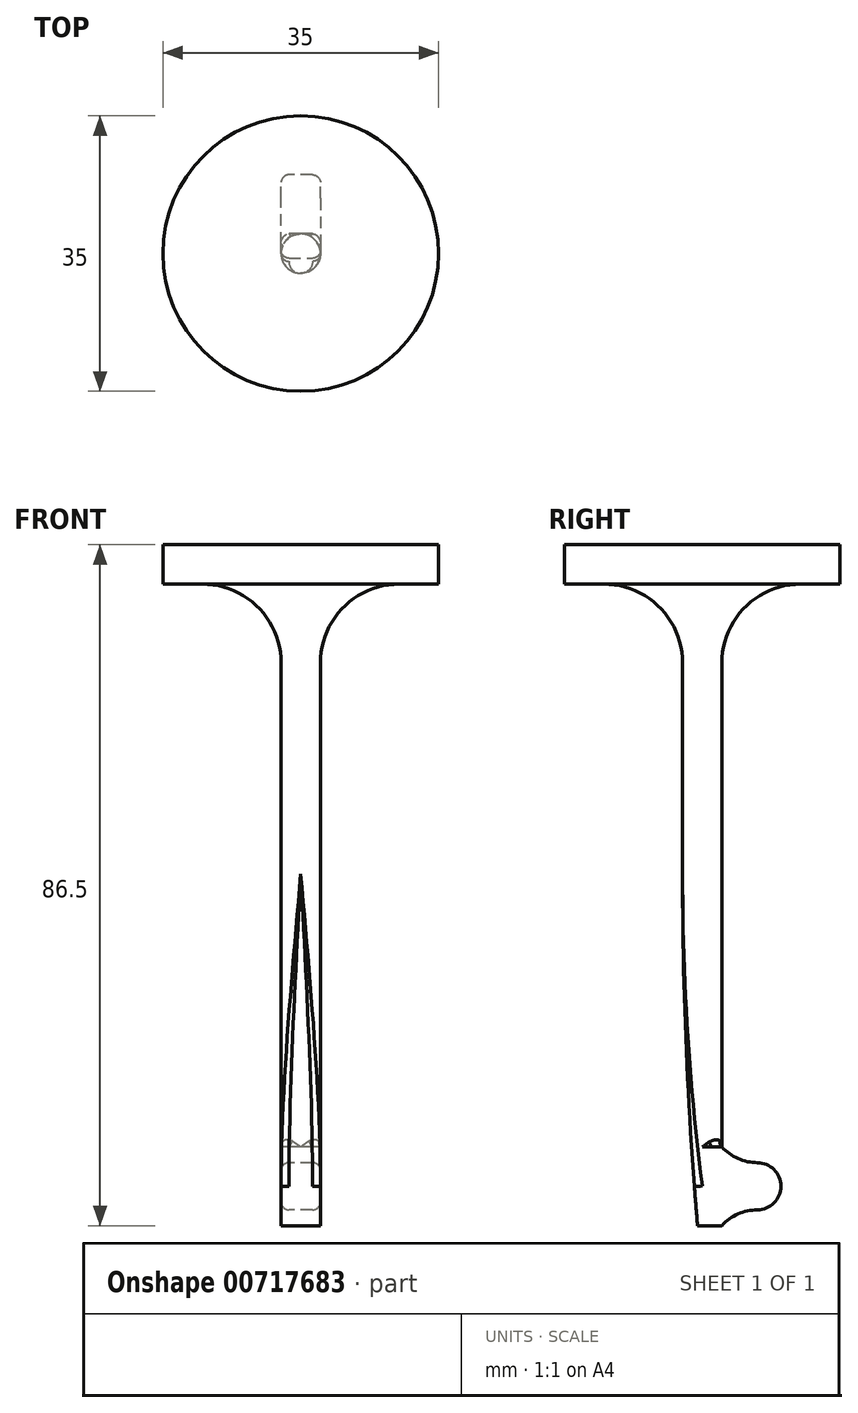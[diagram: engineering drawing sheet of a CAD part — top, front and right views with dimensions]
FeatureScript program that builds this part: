
annotation { "Feature Type Name" : "Feature", "Feature Type Description" : "" }
export const myFeature = defineFeature(function(context is Context, id is Id, definition is map)
    precondition{}
    {
        {
            assignVariable(context, id + "F0", {"name" : "Daxe", "anyValue" : 5});
        }
        {
            var Q0;
            Q0=qCreatedBy(makeId("Front.planeOp"),FACE);
            var sketch = newSketch(context, id + "F1", { "sketchPlane" : qUnion([Q0])});
            skLineSegment(sketch, "E0", {"start": v(-2.5, 81.5) * mm, "end": v(-17.5, 81.5) * mm});
            skLineSegment(sketch, "E1", {"start": v(-17.5, 81.5) * mm, "end": v(-17.5, 86.5) * mm});
            skLineSegment(sketch, "E2", {"start": v(-17.5, 86.5) * mm, "end": v(0, 86.5) * mm});
            skLineSegment(sketch, "E3", {"start": v(0, 86.5) * mm, "end": v(0, 0) * mm});
            skLineSegment(sketch, "E4", {"start": v(0, 0) * mm, "end": v(-2.5, 0) * mm});
            skLineSegment(sketch, "E5", {"start": v(-2.5, 0) * mm, "end": v(-2.5, 81.5) * mm});
            skSolve(sketch);
        }
        {
            var Q0;
            Q0=makeQuery(id+"F1.imprint","IMPRINT",FACE,{"disambiguationData":[TD([[makeQuery(id+"F1.imprint","IMPRINT",EDGE,{"derivedFrom":sQuery(id+"F1.wireOp",EDGE,"E0")}),-1.0]])]});
            var Q1;
            Q1=sQuery(id+"F1.wireOp",EDGE,"E3");
            revolve(context, id + "F2", {"surfaceOperationType" : NewSurfaceOperationType.NEW, "entities" : qUnion([Q0]), "axis" : qUnion([Q1]), "revolveType" : RevolveType.FULL});
        }
        {
            var Q0;
            Q0=qCreatedBy(makeId("Right.planeOp"),FACE);
            var sketch = newSketch(context, id + "F3", { "sketchPlane" : qUnion([Q0])});
            skArc(sketch, "E6", {"start": v(2.5, 10) * mm, "mid": v(4.54, 8.52) * mm, "end": v(7, 8) * mm});
            skArc(sketch, "E7", {"start": v(10, 5) * mm, "mid": v(9.12, 7.12) * mm, "end": v(7, 8) * mm});
            skLineSegment(sketch, "E8", {"start": v(0, 5) * mm, "end": v(10, 5) * mm, "construction": true});
            skLineSegment(sketch, "E9", {"start": v(2.5, 89) * mm, "end": v(2.5, 0) * mm, "construction": true});
            skLineSegment(sketch, "E10", {"start": v(-2.5, 0) * mm, "end": v(-2.5, 89) * mm, "construction": true});
            skArc(sketch, "E11.MirrorCS", {"start": v(10, 5) * mm, "mid": v(9.12, 2.88) * mm, "end": v(7, 2) * mm});
            skArc(sketch, "E12.MirrorCS", {"start": v(2.5, 0) * mm, "mid": v(4.54, 1.48) * mm, "end": v(7, 2) * mm});
            skLineSegment(sketch, "E13", {"start": v(2.5, 10) * mm, "end": v(0, 10) * mm});
            skLineSegment(sketch, "E14", {"start": v(0, 10) * mm, "end": v(0, 0) * mm});
            skLineSegment(sketch, "E15", {"start": v(0, 0) * mm, "end": v(2.5, 0) * mm});
            skSolve(sketch);
        }
        {
            var Q0;
            Q0=makeQuery(id+"F3.imprint","IMPRINT",FACE,{"disambiguationData":[TD([[makeQuery(id+"F3.imprint","IMPRINT",EDGE,{"derivedFrom":sQuery(id+"F3.wireOp",EDGE,"E6")}),-1.0]])]});
            extrude(context, id + "F4", {"entities" : qUnion([Q0]), "operationType" : NewBodyOperationType.ADD, "endBound" : BoundingType.SYMMETRIC, "depth" : (getVariable(context, 'Daxe')) * mm, "offsetDistance" : 25 * mm});
        }
        {
            var Q0;
            Q0=makeQuery(id+"F4.opExtrude","CAP_EDGE",EDGE,{"disambiguationData":[OSD([sQuery(id+"F3.wireOp",EDGE,"E6")])],"isStart":false});
            var Q1;
            Q1=makeQuery(id+"F4.opExtrude","CAP_EDGE",EDGE,{"disambiguationData":[OSD([sQuery(id+"F3.wireOp",EDGE,"E7"),sQuery(id+"F3.wireOp",EDGE,"E11.MirrorCS")])],"isStart":false});
            var Q2;
            Q2=makeQuery(id+"F4.opExtrude","CAP_EDGE",EDGE,{"disambiguationData":[OSD([sQuery(id+"F3.wireOp",EDGE,"E6")])],"isStart":true});
            fillet(context, id + "F5", {"entities" : qUnion([Q0, Q1, Q2]), "radius" : 1 * mm, "tangentPropagation" : true, "allowEdgeOverflow" : false});
        }
        {
            var Q0;
            Q0=makeQuery(id+"F2.opRevolve","SWEPT_EDGE",EDGE,{"disambiguationData":[OSD([sQuery(id+"F1.wireOp",EDGE,"E0"),sQuery(id+"F1.wireOp",EDGE,"E5")])]});
            fillet(context, id + "F6", {"entities" : qUnion([Q0]), "radius" : 10 * mm, "tangentPropagation" : true, "allowEdgeOverflow" : false});
        }
        {
            var Q0;
            Q0=qCreatedBy(makeId("Right.planeOp"),FACE);
            var sketch = newSketch(context, id + "F7", { "sketchPlane" : qUnion([Q0])});
            skArc(sketch, "E16", {"start": v(2.5, 10) * mm, "mid": v(4.54, 8.52) * mm, "end": v(7, 8) * mm});
            skArc(sketch, "E17", {"start": v(7, 2) * mm, "mid": v(10, 5) * mm, "end": v(7, 8) * mm});
            skArc(sketch, "E18", {"start": v(7, 2) * mm, "mid": v(4.54, 1.48) * mm, "end": v(2.5, 0) * mm});
            skSolve(sketch);
        }
        {
            var Q0;
            Q0=makeQuery(id+"F4.boolean.opBoolean","INTERSECT",EDGE,{"disambiguationData":[OD(1.0)],"derivedFrom":[makeQuery(id+"F2.opRevolve","SWEPT_FACE",FACE,{"disambiguationData":[OSD([sQuery(id+"F1.wireOp",EDGE,"E5")])]}),makeQuery(id+"F4.opExtrude","SWEPT_FACE",FACE,{"disambiguationData":[OSD([sQuery(id+"F3.wireOp",EDGE,"E13")])]})]});
            fillet(context, id + "F8", {"entities" : qUnion([Q0]), "radius" : 1 * mm, "tangentPropagation" : true, "allowEdgeOverflow" : false});
        }
        {
            var Q0;
            Q0=qCreatedBy(makeId("Right.planeOp"),FACE);
            var sketch = newSketch(context, id + "F9", { "sketchPlane" : qUnion([Q0])});
            skArc(sketch, "E19", {"start": v(-2.5, 44.66) * mm, "mid": v(-2.02, 22.3) * mm, "end": v(-0.6, 0) * mm});
            skLineSegment(sketch, "E20", {"start": v(-2.5, 0) * mm, "end": v(-2.5, 71.5) * mm, "construction": true});
            skLineSegment(sketch, "E21", {"start": v(2.5, 71.5) * mm, "end": v(2.5, 10) * mm, "construction": true});
            skLineSegment(sketch, "E22", {"start": v(-1, 5) * mm, "end": v(10, 5) * mm, "construction": true});
            skLineSegment(sketch, "E23", {"start": v(-2.5, 0) * mm, "end": v(-0.6, 0) * mm});
            skLineSegment(sketch, "E24", {"start": v(-2.5, 0) * mm, "end": v(-2.5, 44.66) * mm});
            skSolve(sketch);
        }
        {
            var Q0;
            Q0 = qSketchRegion(id + "F9", true);
            extrude(context, id + "F10", {"entities" : qUnion([Q0]), "operationType" : NewBodyOperationType.REMOVE, "endBound" : BoundingType.SYMMETRIC, "oppositeDirection" : true, "depth" : 10 * mm, "offsetDistance" : 25 * mm});
        }
        {
            var Q0;
            Q0=makeQuery(id+"F10.boolean.opBoolean","INTERSECT",EDGE,{"disambiguationData":[OD(1.0)],"derivedFrom":[makeQuery(id+"F2.opRevolve","SWEPT_FACE",FACE,{"disambiguationData":[OSD([sQuery(id+"F1.wireOp",EDGE,"E5")])]}),makeQuery(id+"F10.opExtrude","SWEPT_FACE",FACE,{"disambiguationData":[OSD([sQuery(id+"F9.wireOp",EDGE,"E19")])]})]});
            var Q1;
            Q1=makeQuery(id+"F10.boolean.opBoolean","INTERSECT",EDGE,{"disambiguationData":[OD(0.0)],"derivedFrom":[makeQuery(id+"F2.opRevolve","SWEPT_FACE",FACE,{"disambiguationData":[OSD([sQuery(id+"F1.wireOp",EDGE,"E5")])]}),makeQuery(id+"F10.opExtrude","SWEPT_FACE",FACE,{"disambiguationData":[OSD([sQuery(id+"F9.wireOp",EDGE,"E19")])]})]});
            fillet(context, id + "F11", {"entities" : qUnion([Q0, Q1]), "radius" : 1 * mm, "tangentPropagation" : true, "allowEdgeOverflow" : false});
        }
    });
